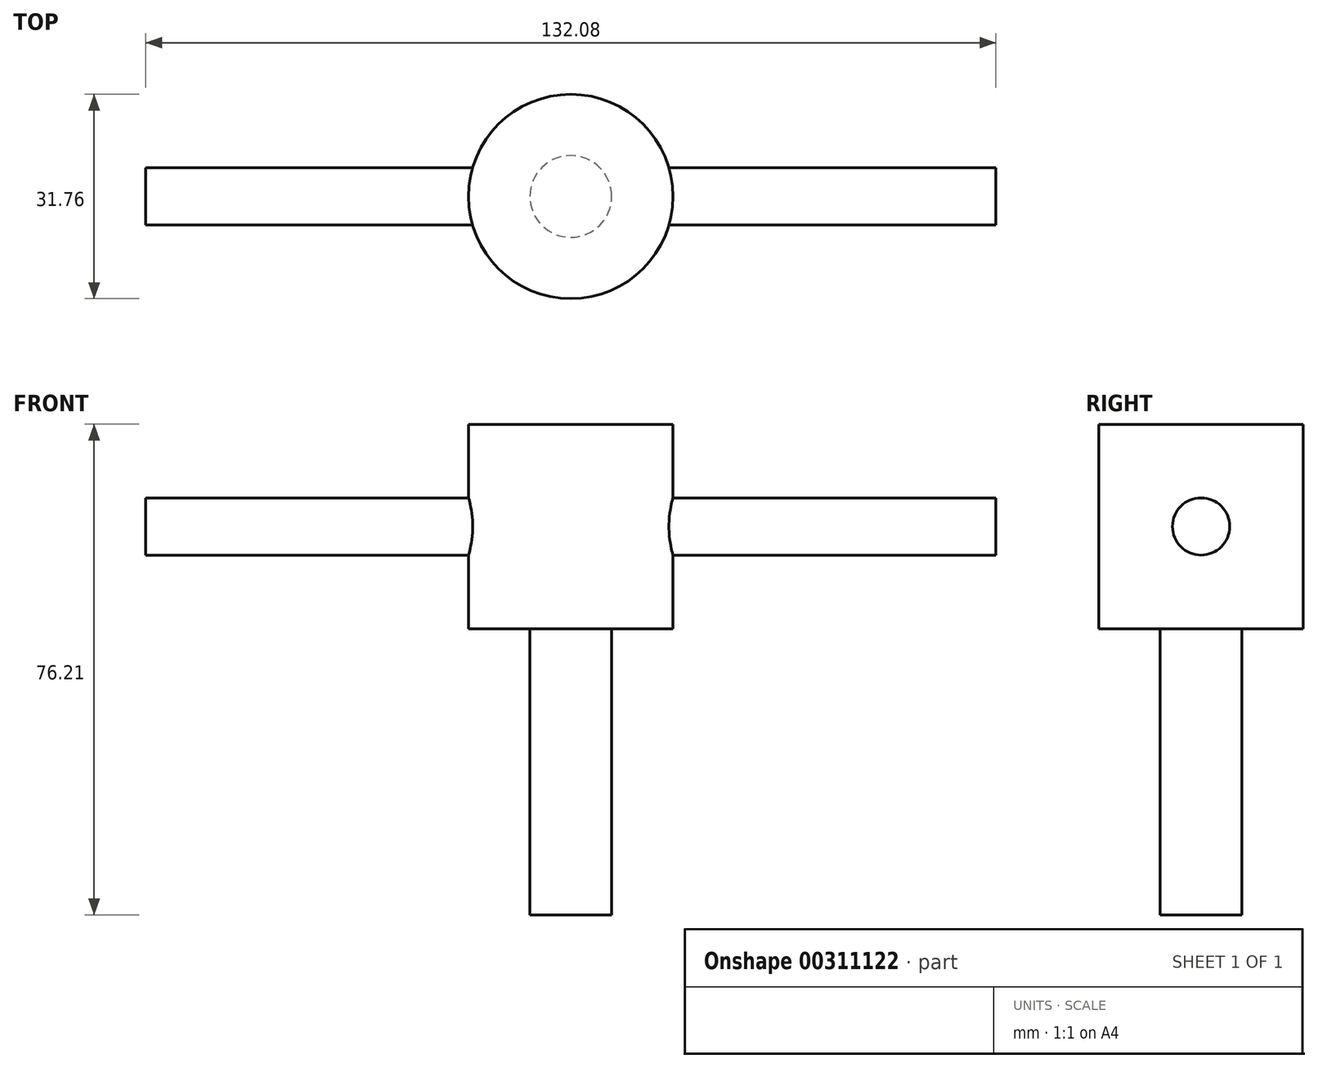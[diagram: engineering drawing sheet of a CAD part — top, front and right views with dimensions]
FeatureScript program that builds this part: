
annotation { "Feature Type Name" : "Feature", "Feature Type Description" : "" }
export const myFeature = defineFeature(function(context is Context, id is Id, definition is map)
    precondition{}
    {
        {
            var Q0;
            Q0=qCreatedBy(makeId("Top.planeOp"),FACE);
            var sketch = newSketch(context, id + "F0", { "sketchPlane" : qUnion([Q0])});
            skCircle(sketch, "E0", {"center": v(0, 0) * mm, "radius": 15.88 * mm});
            skSolve(sketch);
        }
        {
            var Q0;
            Q0 = qSketchRegion(id + "F0", true);
            extrude(context, id + "F1", {"entities" : qUnion([Q0]), "endBound" : BoundingType.SYMMETRIC, "oppositeDirection" : true, "depth" : 31.75 * mm});
        }
        {
            var Q0;
            Q0=makeQuery(id+"F1.opExtrude","CAP_FACE",FACE,{"disambiguationData":[OSD([sQuery(id+"F0.wireOp",EDGE,"E0")])],"isStart":false});
            var sketch = newSketch(context, id + "F2", { "sketchPlane" : qUnion([Q0])});
            skCircle(sketch, "E1", {"center": v(0, 0) * mm, "radius": 6.35 * mm});
            skSolve(sketch);
        }
        {
            var Q0;
            Q0 = qSketchRegion(id + "F2", true);
            extrude(context, id + "F3", {"entities" : qUnion([Q0]), "operationType" : NewBodyOperationType.ADD, "depth" : 44.45 * mm});
        }
        {
            var Q0;
            Q0=qCreatedBy(makeId("Right.planeOp"),FACE);
            var sketch = newSketch(context, id + "F4", { "sketchPlane" : qUnion([Q0])});
            skCircle(sketch, "E2", {"center": v(0, 0) * mm, "radius": 4.45 * mm});
            skSolve(sketch);
        }
        {
            var Q0;
            Q0 = qSketchRegion(id + "F4", true);
            extrude(context, id + "F5", {"entities" : qUnion([Q0]), "operationType" : NewBodyOperationType.ADD, "endBound" : BoundingType.SYMMETRIC, "depth" : 132.08 * mm});
        }
    });
